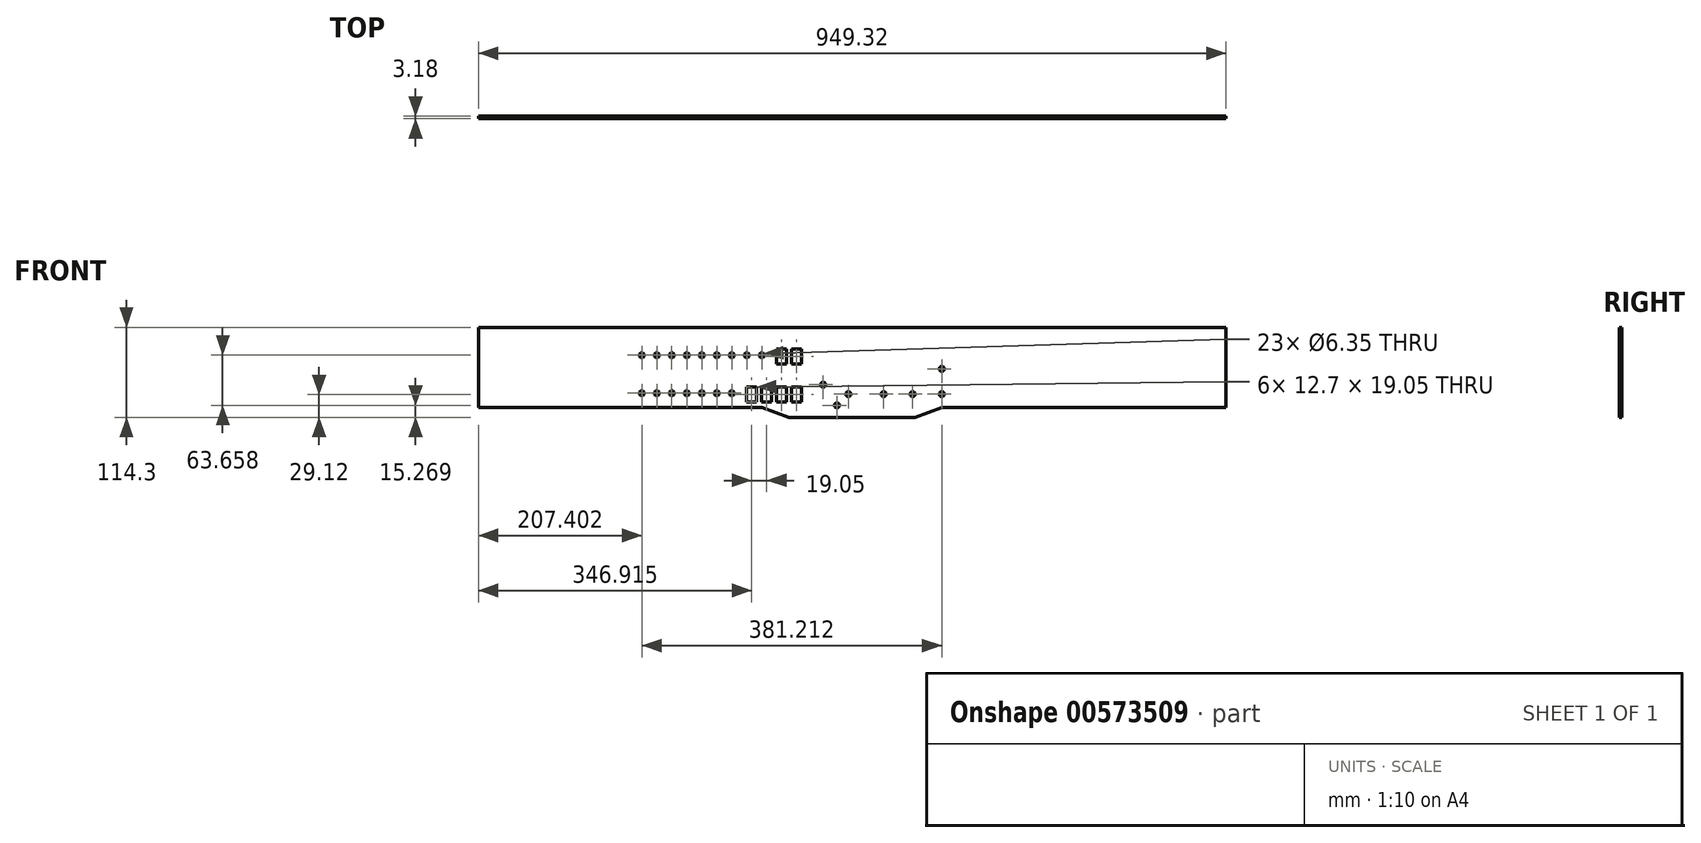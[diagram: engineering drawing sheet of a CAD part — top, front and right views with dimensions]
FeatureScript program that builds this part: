
annotation { "Feature Type Name" : "Feature", "Feature Type Description" : "" }
export const myFeature = defineFeature(function(context is Context, id is Id, definition is map)
    precondition{}
    {
        {
            var Q0;
            Q0=qCreatedBy(makeId("Front.planeOp"),FACE);
            var sketch = newSketch(context, id + "F0", { "sketchPlane" : qUnion([Q0])});
            skLineSegment(sketch, "E0", {"start": v(25.4, 0) * mm, "end": v(974.73, 0) * mm});
            skLineSegment(sketch, "E1", {"start": v(974.73, 0) * mm, "end": v(974.73, -101.6) * mm});
            skLineSegment(sketch, "E2", {"start": v(974.73, -101.6) * mm, "end": v(614.36, -101.6) * mm});
            skLineSegment(sketch, "E3", {"start": v(614.36, -101.6) * mm, "end": v(580.07, -114.3) * mm});
            skLineSegment(sketch, "E4", {"start": v(580.07, -114.3) * mm, "end": v(420.05, -114.3) * mm});
            skLineSegment(sketch, "E5", {"start": v(420.05, -114.3) * mm, "end": v(385.76, -101.6) * mm});
            skLineSegment(sketch, "E6", {"start": v(385.76, -101.6) * mm, "end": v(25.4, -101.6) * mm});
            skLineSegment(sketch, "E7", {"start": v(25.4, -101.6) * mm, "end": v(25.4, 0) * mm});
            skPoint(sketch, "E8", {"position": v(500.06, 0) * mm});
            skPoint(sketch, "E9", {"position": v(500.06, -114.3) * mm});
            skCircle(sketch, "E10", {"center": v(614.01, -84.73) * mm, "radius": 3.18 * mm});
            skCircle(sketch, "E11", {"center": v(614.01, -52.8) * mm, "radius": 3.18 * mm});
            skCircle(sketch, "E12", {"center": v(576.75, -84.73) * mm, "radius": 3.18 * mm});
            skCircle(sketch, "E13", {"center": v(539.95, -84.73) * mm, "radius": 3.18 * mm});
            skCircle(sketch, "E14", {"center": v(495.25, -84.73) * mm, "radius": 3.18 * mm});
            skCircle(sketch, "E15", {"center": v(463.12, -72.8) * mm, "radius": 3.18 * mm});
            skCircle(sketch, "E16", {"center": v(480.7, -99.03) * mm, "radius": 3.18 * mm});
            skLineSegment(sketch, "E17.bottom", {"start": v(423.11, -27.4) * mm, "end": v(435.81, -27.4) * mm});
            skLineSegment(sketch, "E17.top", {"start": v(423.11, -46.45) * mm, "end": v(435.81, -46.45) * mm});
            skLineSegment(sketch, "E17.left", {"start": v(423.11, -27.4) * mm, "end": v(423.11, -46.45) * mm});
            skLineSegment(sketch, "E17.right", {"start": v(435.81, -27.4) * mm, "end": v(435.81, -46.45) * mm});
            skLineSegment(sketch, "E18.0.1.0", {"start": v(423.11, -75.66) * mm, "end": v(435.81, -75.66) * mm});
            skLineSegment(sketch, "E18.0.1.1", {"start": v(423.11, -94.7) * mm, "end": v(435.81, -94.7) * mm});
            skLineSegment(sketch, "E18.0.1.2", {"start": v(423.11, -75.66) * mm, "end": v(423.11, -94.7) * mm});
            skLineSegment(sketch, "E18.0.1.3", {"start": v(435.81, -75.66) * mm, "end": v(435.81, -94.7) * mm});
            skLineSegment(sketch, "E18.1.0.0", {"start": v(404.06, -27.4) * mm, "end": v(416.76, -27.4) * mm});
            skLineSegment(sketch, "E18.1.0.1", {"start": v(404.06, -46.45) * mm, "end": v(416.76, -46.45) * mm});
            skLineSegment(sketch, "E18.1.0.2", {"start": v(404.06, -27.4) * mm, "end": v(404.06, -46.45) * mm});
            skLineSegment(sketch, "E18.1.0.3", {"start": v(416.76, -27.4) * mm, "end": v(416.76, -46.45) * mm});
            skLineSegment(sketch, "E18.1.1.0", {"start": v(404.06, -75.66) * mm, "end": v(416.76, -75.66) * mm});
            skLineSegment(sketch, "E18.1.1.1", {"start": v(404.06, -94.7) * mm, "end": v(416.76, -94.7) * mm});
            skLineSegment(sketch, "E18.1.1.2", {"start": v(404.06, -75.66) * mm, "end": v(404.06, -94.7) * mm});
            skLineSegment(sketch, "E18.1.1.3", {"start": v(416.76, -75.66) * mm, "end": v(416.76, -94.7) * mm});
            skLineSegment(sketch, "E18.direction1", {"start": v(423.11, -46.45) * mm, "end": v(404.06, -46.45) * mm, "construction": true});
            skLineSegment(sketch, "E18.direction2", {"start": v(423.11, -46.45) * mm, "end": v(423.11, -94.7) * mm, "construction": true});
            skLineSegment(sketch, "E19.0.2.1", {"start": v(385.01, -75.66) * mm, "end": v(397.71, -75.66) * mm});
            skLineSegment(sketch, "E19.3.2.1", {"start": v(385.01, -94.7) * mm, "end": v(397.71, -94.7) * mm});
            skLineSegment(sketch, "E19.6.2.1", {"start": v(385.01, -75.66) * mm, "end": v(385.01, -94.7) * mm});
            skLineSegment(sketch, "E19.9.2.1", {"start": v(397.71, -75.66) * mm, "end": v(397.71, -94.7) * mm});
            skLineSegment(sketch, "E19.0.3.1", {"start": v(365.96, -75.66) * mm, "end": v(378.66, -75.66) * mm});
            skLineSegment(sketch, "E19.3.3.1", {"start": v(365.96, -94.7) * mm, "end": v(378.66, -94.7) * mm});
            skLineSegment(sketch, "E19.6.3.1", {"start": v(365.96, -75.66) * mm, "end": v(365.96, -94.7) * mm});
            skLineSegment(sketch, "E19.9.3.1", {"start": v(378.66, -75.66) * mm, "end": v(378.66, -94.7) * mm});
            skCircle(sketch, "E20", {"center": v(385.2, -35.37) * mm, "radius": 3.18 * mm});
            skCircle(sketch, "E21.1.0.0", {"center": v(366.15, -35.37) * mm, "radius": 3.18 * mm});
            skCircle(sketch, "E21.2.0.0", {"center": v(347.1, -35.37) * mm, "radius": 3.18 * mm});
            skCircle(sketch, "E21.2.1.0", {"center": v(347.1, -83.63) * mm, "radius": 3.18 * mm});
            skCircle(sketch, "E21.3.0.0", {"center": v(328.05, -35.37) * mm, "radius": 3.18 * mm});
            skCircle(sketch, "E21.3.1.0", {"center": v(328.05, -83.63) * mm, "radius": 3.18 * mm});
            skCircle(sketch, "E21.4.0.0", {"center": v(309, -35.37) * mm, "radius": 3.18 * mm});
            skCircle(sketch, "E21.4.1.0", {"center": v(309, -83.63) * mm, "radius": 3.18 * mm});
            skCircle(sketch, "E21.5.0.0", {"center": v(289.95, -35.37) * mm, "radius": 3.18 * mm});
            skCircle(sketch, "E21.5.1.0", {"center": v(289.95, -83.63) * mm, "radius": 3.18 * mm});
            skCircle(sketch, "E21.6.0.0", {"center": v(270.9, -35.37) * mm, "radius": 3.18 * mm});
            skCircle(sketch, "E21.6.1.0", {"center": v(270.9, -83.63) * mm, "radius": 3.18 * mm});
            skCircle(sketch, "E21.7.0.0", {"center": v(251.85, -35.37) * mm, "radius": 3.18 * mm});
            skCircle(sketch, "E21.7.1.0", {"center": v(251.85, -83.63) * mm, "radius": 3.18 * mm});
            skCircle(sketch, "E21.8.0.0", {"center": v(232.8, -35.37) * mm, "radius": 3.18 * mm});
            skCircle(sketch, "E21.8.1.0", {"center": v(232.8, -83.63) * mm, "radius": 3.18 * mm});
            skLineSegment(sketch, "E21.direction1", {"start": v(385.2, -35.37) * mm, "end": v(366.15, -35.37) * mm, "construction": true});
            skLineSegment(sketch, "E21.direction2", {"start": v(385.2, -35.37) * mm, "end": v(385.2, -83.63) * mm, "construction": true});
            skSolve(sketch);
        }
        {
            var Q0;
            Q0 = qSketchRegion(id + "F0", true);
            extrude(context, id + "F1", {"entities" : qUnion([Q0]), "oppositeDirection" : true, "depth" : 3.17 * mm, "offsetDistance" : 25.4 * mm});
        }
    });
